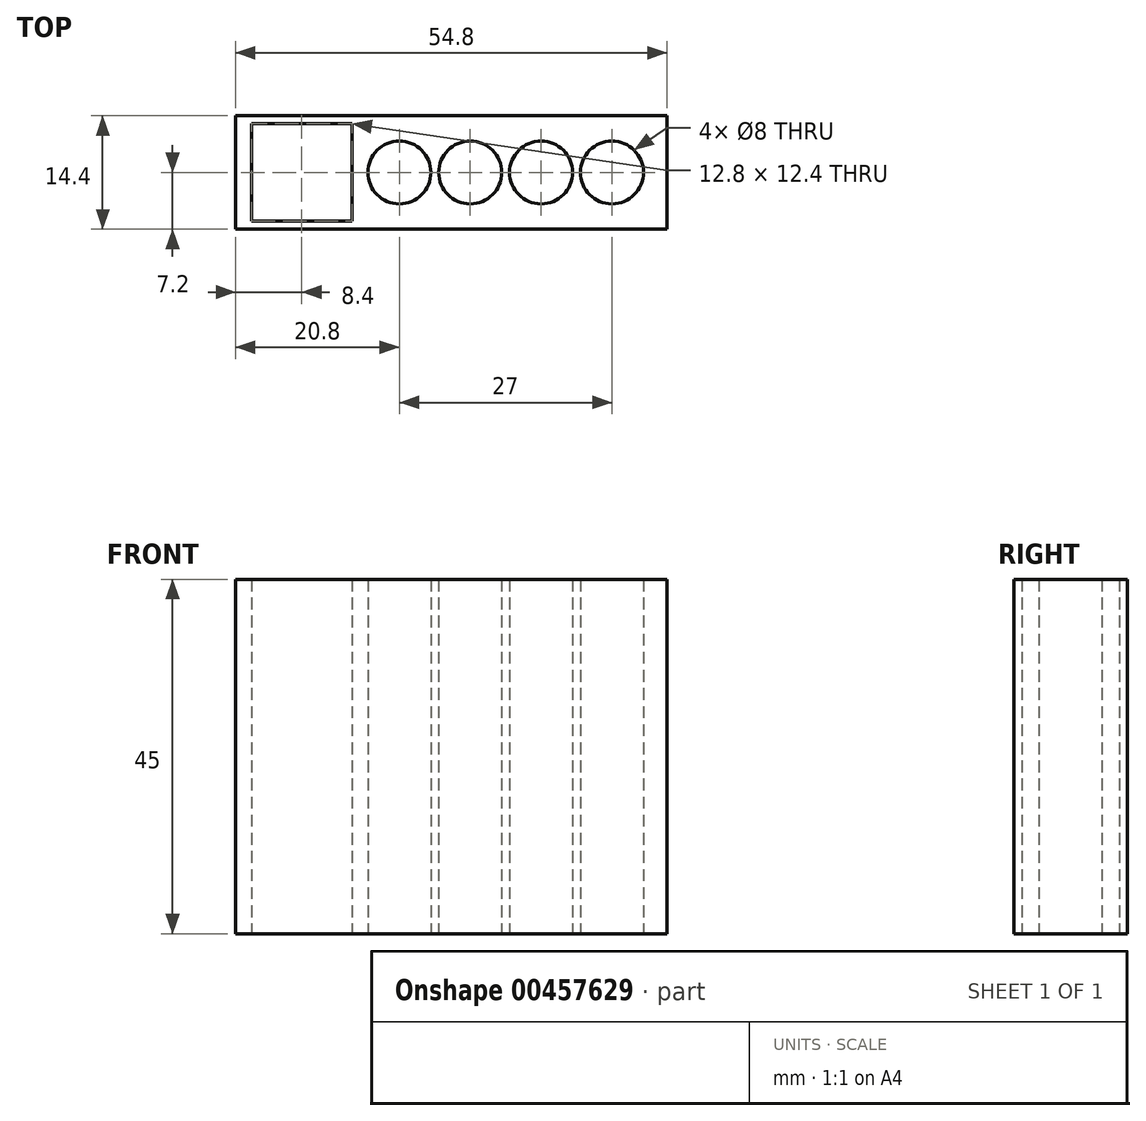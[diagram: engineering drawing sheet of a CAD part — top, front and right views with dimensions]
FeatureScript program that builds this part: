
annotation { "Feature Type Name" : "Feature", "Feature Type Description" : "" }
export const myFeature = defineFeature(function(context is Context, id is Id, definition is map)
    precondition{}
    {
        {
            var Q0;
            Q0=qCreatedBy(makeId("Top.planeOp"),FACE);
            var sketch = newSketch(context, id + "F0", { "sketchPlane" : qUnion([Q0])});
            skLineSegment(sketch, "E0.bottom", {"start": v(-47.8, 7.2) * mm, "end": v(7, 7.2) * mm});
            skLineSegment(sketch, "E0.top", {"start": v(-47.8, -7.2) * mm, "end": v(7, -7.2) * mm});
            skLineSegment(sketch, "E0.left", {"start": v(-47.8, 7.2) * mm, "end": v(-47.8, -7.2) * mm});
            skLineSegment(sketch, "E0.right", {"start": v(7, 7.2) * mm, "end": v(7, -7.2) * mm});
            skCircle(sketch, "E1", {"center": v(-27, 0) * mm, "radius": 4 * mm});
            skCircle(sketch, "E2", {"center": v(-18, 0) * mm, "radius": 4 * mm});
            skCircle(sketch, "E3", {"center": v(0, 0) * mm, "radius": 4 * mm});
            skLineSegment(sketch, "E4.bottom", {"start": v(-45.8, 6.2) * mm, "end": v(-33, 6.2) * mm});
            skLineSegment(sketch, "E4.top", {"start": v(-45.8, -6.2) * mm, "end": v(-33, -6.2) * mm});
            skLineSegment(sketch, "E4.left", {"start": v(-45.8, 6.2) * mm, "end": v(-45.8, -6.2) * mm});
            skLineSegment(sketch, "E4.right", {"start": v(-33, 6.2) * mm, "end": v(-33, -6.2) * mm});
            skCircle(sketch, "E5", {"center": v(-9, 0) * mm, "radius": 4 * mm});
            skSolve(sketch);
        }
        {
            var Q0;
            Q0=makeQuery(id+"F0.imprint","IMPRINT",FACE,{"disambiguationData":[TD([[makeQuery(id+"F0.imprint","IMPRINT",EDGE,{"derivedFrom":sQuery(id+"F0.wireOp",EDGE,"E0.bottom")}),-1.0]])]});
            extrude(context, id + "F1", {"entities" : qUnion([Q0]), "depth" : 45 * mm});
        }
    });
